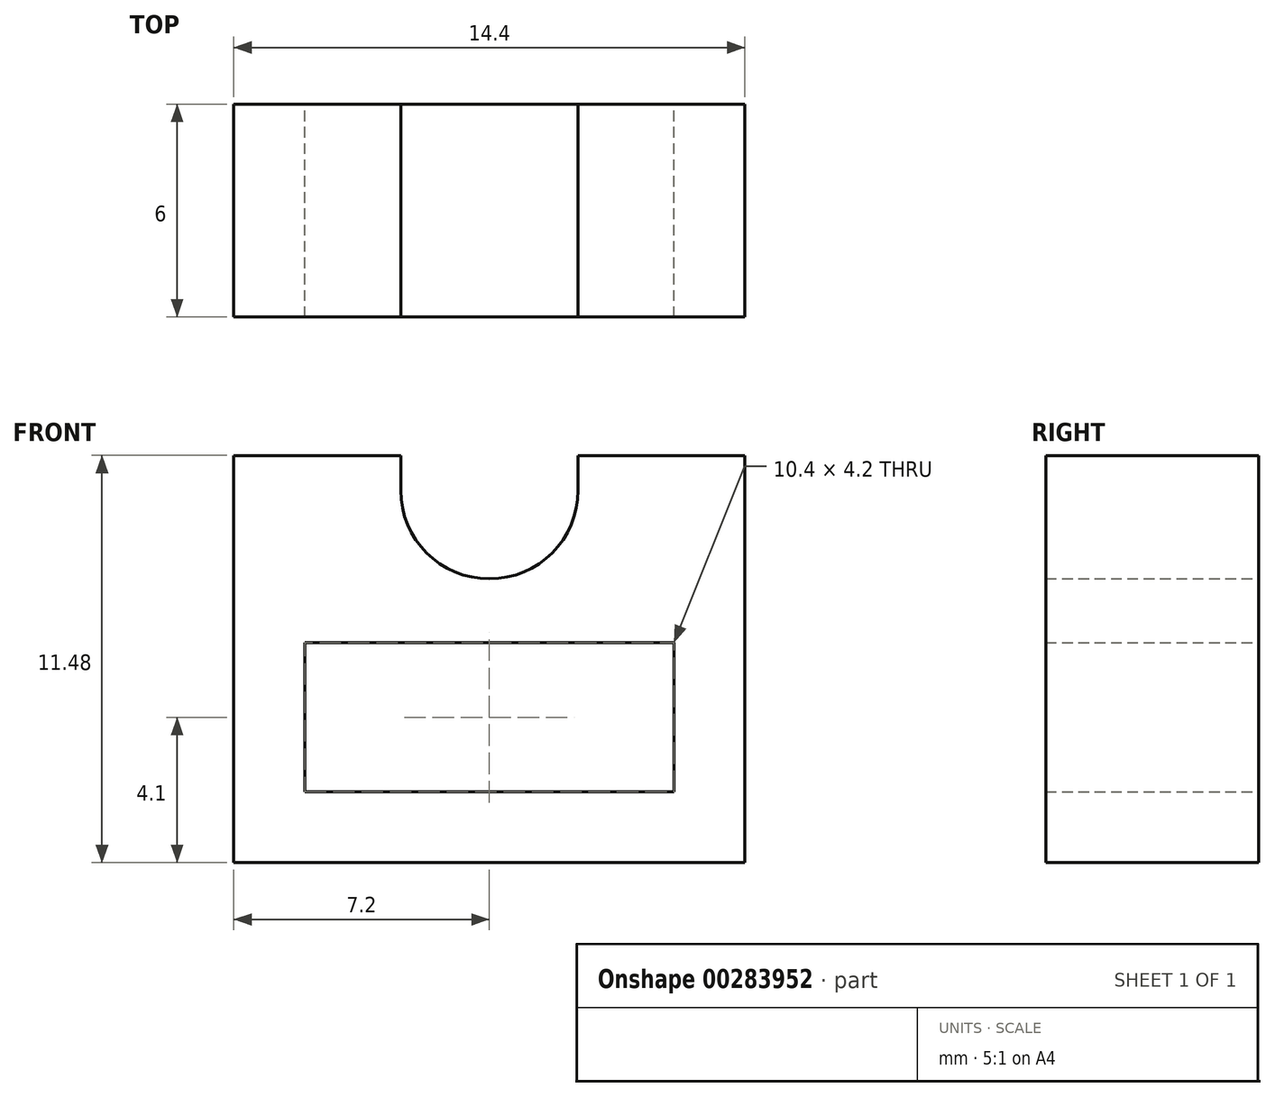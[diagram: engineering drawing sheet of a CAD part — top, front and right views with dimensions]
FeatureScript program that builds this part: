
annotation { "Feature Type Name" : "Feature", "Feature Type Description" : "" }
export const myFeature = defineFeature(function(context is Context, id is Id, definition is map)
    precondition{}
    {
        {
            var Q0;
            Q0=qCreatedBy(makeId("Front.planeOp"),FACE);
            var sketch = newSketch(context, id + "F0", { "sketchPlane" : qUnion([Q0])});
            skLineSegment(sketch, "E0.bottom", {"start": v(0, 0) * mm, "end": v(10.4, 0) * mm});
            skLineSegment(sketch, "E0.top", {"start": v(0, 4.2) * mm, "end": v(10.4, 4.2) * mm});
            skLineSegment(sketch, "E0.left", {"start": v(0, 0) * mm, "end": v(0, 4.2) * mm});
            skLineSegment(sketch, "E0.right", {"start": v(10.4, 0) * mm, "end": v(10.4, 4.2) * mm});
            skLineSegment(sketch, "E1.bottom", {"start": v(-2, -2) * mm, "end": v(12.4, -2) * mm});
            skLineSegment(sketch, "E1.left", {"start": v(-2, -2) * mm, "end": v(-2, 6) * mm});
            skLineSegment(sketch, "E1.right", {"start": v(12.4, -2) * mm, "end": v(12.4, 6) * mm});
            skArc(sketch, "E2", {"start": v(2.7, 8.5) * mm, "mid": v(5.2, 6) * mm, "end": v(7.7, 8.5) * mm});
            skPoint(sketch, "E2.centerSnap0", {"position": v(5.2, 6) * mm});
            skLineSegment(sketch, "E3", {"start": v(12.4, 6) * mm, "end": v(12.4, 8.5) * mm});
            skLineSegment(sketch, "E4", {"start": v(5.2, -2) * mm, "end": v(5.2, 0) * mm, "construction": true});
            skLineSegment(sketch, "E5.MirrorCS", {"start": v(-2, 6) * mm, "end": v(-2, 8.5) * mm});
            skLineSegment(sketch, "E6", {"start": v(2.7, 8.5) * mm, "end": v(2.7, 9.48) * mm});
            skLineSegment(sketch, "E7", {"start": v(2.7, 9.48) * mm, "end": v(-2, 9.48) * mm});
            skLineSegment(sketch, "E8", {"start": v(-2, 9.48) * mm, "end": v(-2, 8.5) * mm});
            skLineSegment(sketch, "E9.MirrorCS", {"start": v(7.7, 8.5) * mm, "end": v(7.7, 9.48) * mm});
            skLineSegment(sketch, "E10.MirrorCS", {"start": v(7.7, 9.48) * mm, "end": v(12.4, 9.48) * mm});
            skLineSegment(sketch, "E11.MirrorCS", {"start": v(12.4, 9.48) * mm, "end": v(12.4, 8.5) * mm});
            skSolve(sketch);
        }
        {
            var Q0;
            Q0 = qSketchRegion(id + "F0", true);
            extrude(context, id + "F1", {"entities" : qUnion([Q0]), "depth" : 6 * mm});
        }
    });
